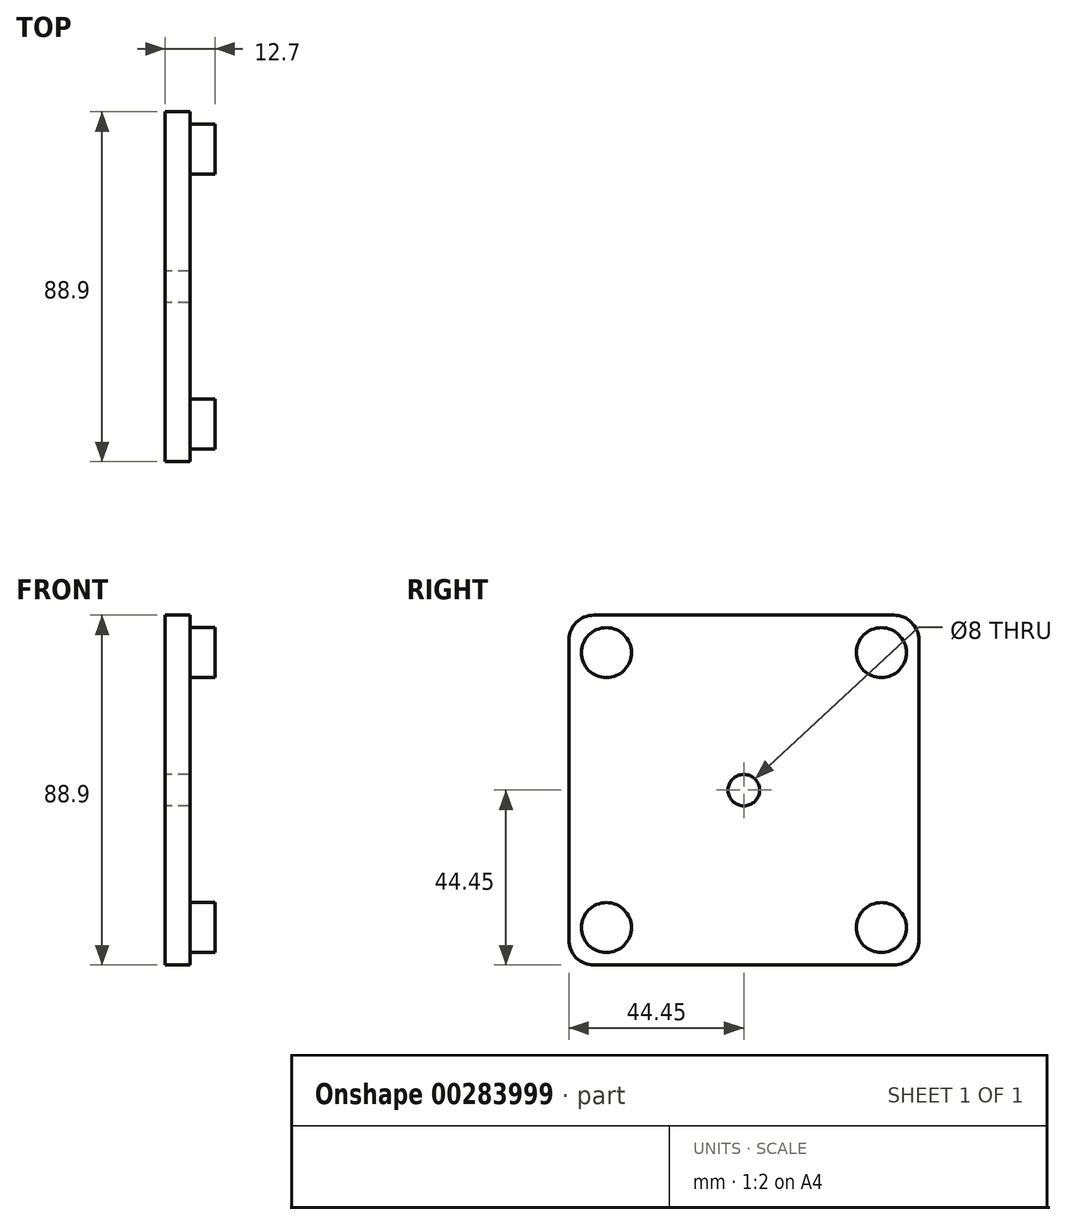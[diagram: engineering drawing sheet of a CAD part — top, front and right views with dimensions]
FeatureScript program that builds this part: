
annotation { "Feature Type Name" : "Feature", "Feature Type Description" : "" }
export const myFeature = defineFeature(function(context is Context, id is Id, definition is map)
    precondition{}
    {
        {
            var Q0;
            Q0=qCreatedBy(makeId("Right.planeOp"),FACE);
            var sketch = newSketch(context, id + "F0", { "sketchPlane" : qUnion([Q0])});
            skLineSegment(sketch, "E0.bottom", {"start": v(38.1, -44.45) * mm, "end": v(-38.1, -44.45) * mm});
            skLineSegment(sketch, "E0.top", {"start": v(38.1, 44.45) * mm, "end": v(-38.1, 44.45) * mm});
            skLineSegment(sketch, "E0.left", {"start": v(44.45, -38.1) * mm, "end": v(44.45, 38.1) * mm});
            skLineSegment(sketch, "E0.right", {"start": v(-44.45, -38.1) * mm, "end": v(-44.45, 38.1) * mm});
            skPoint(sketch, "E1.visualSharp", {"position": v(-44.45, -44.45) * mm});
            skArc(sketch, "E1.filletArc", {"start": v(-44.45, -38.1) * mm, "mid": v(-42.6, -42.6) * mm, "end": v(-38.1, -44.45) * mm});
            skPoint(sketch, "E2.visualSharp", {"position": v(-44.45, 44.45) * mm});
            skArc(sketch, "E2.filletArc", {"start": v(-38.1, 44.45) * mm, "mid": v(-42.6, 42.6) * mm, "end": v(-44.45, 38.1) * mm});
            skPoint(sketch, "E3.visualSharp", {"position": v(44.45, 44.45) * mm});
            skArc(sketch, "E3.filletArc", {"start": v(44.45, 38.1) * mm, "mid": v(42.6, 42.6) * mm, "end": v(38.1, 44.45) * mm});
            skPoint(sketch, "E4.visualSharp", {"position": v(44.45, -44.45) * mm});
            skArc(sketch, "E4.filletArc", {"start": v(38.1, -44.45) * mm, "mid": v(42.6, -42.6) * mm, "end": v(44.45, -38.1) * mm});
            skCircle(sketch, "E5", {"center": v(-34.93, 34.93) * mm, "radius": 6.35 * mm});
            skCircle(sketch, "E6.0.1.0", {"center": v(-34.93, -34.92) * mm, "radius": 6.35 * mm});
            skCircle(sketch, "E6.1.0.0", {"center": v(34.92, 34.93) * mm, "radius": 6.35 * mm});
            skCircle(sketch, "E6.1.1.0", {"center": v(34.92, -34.93) * mm, "radius": 6.35 * mm});
            skLineSegment(sketch, "E6.direction1", {"start": v(-34.93, 34.93) * mm, "end": v(34.92, 34.93) * mm, "construction": true});
            skLineSegment(sketch, "E6.direction2", {"start": v(-34.93, 34.93) * mm, "end": v(-34.93, -34.92) * mm, "construction": true});
            skCircle(sketch, "E7", {"center": v(0, 0) * mm, "radius": 4 * mm});
            skSolve(sketch);
        }
        {
            var Q0;
            Q0=makeQuery(id+"F0.imprint","IMPRINT",FACE,{"disambiguationData":[TD([[makeQuery(id+"F0.imprint","IMPRINT",EDGE,{"derivedFrom":sQuery(id+"F0.wireOp",EDGE,"E0.bottom")}),-1.0]])]});
            extrude(context, id + "F1", {"entities" : qUnion([Q0]), "depth" : 6.35 * mm});
        }
        {
            var Q0;
            Q0=makeQuery(id+"F0.imprint","IMPRINT",FACE,{"disambiguationData":[TD([[makeQuery(id+"F0.imprint","IMPRINT",EDGE,{"derivedFrom":sQuery(id+"F0.wireOp",EDGE,"E5")}),1.0]])]});
            var Q1;
            Q1=makeQuery(id+"F0.imprint","IMPRINT",FACE,{"disambiguationData":[TD([[makeQuery(id+"F0.imprint","IMPRINT",EDGE,{"derivedFrom":sQuery(id+"F0.wireOp",EDGE,"E6.1.0.0")}),1.0]])]});
            var Q2;
            Q2=makeQuery(id+"F0.imprint","IMPRINT",FACE,{"disambiguationData":[TD([[makeQuery(id+"F0.imprint","IMPRINT",EDGE,{"derivedFrom":sQuery(id+"F0.wireOp",EDGE,"E6.1.1.0")}),1.0]])]});
            var Q3;
            Q3=makeQuery(id+"F0.imprint","IMPRINT",FACE,{"disambiguationData":[TD([[makeQuery(id+"F0.imprint","IMPRINT",EDGE,{"derivedFrom":sQuery(id+"F0.wireOp",EDGE,"E6.0.1.0")}),1.0]])]});
            extrude(context, id + "F2", {"entities" : qUnion([Q0, Q1, Q2, Q3]), "operationType" : NewBodyOperationType.ADD, "depth" : 12.7 * mm});
        }
    });
